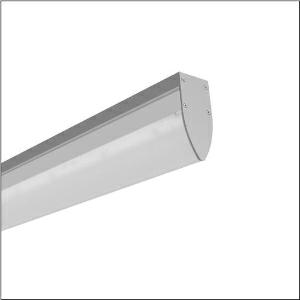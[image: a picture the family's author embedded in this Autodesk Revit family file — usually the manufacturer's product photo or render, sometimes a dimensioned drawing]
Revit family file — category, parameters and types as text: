
# Revit family: mira_r__21_td_51fr527g454a_bdf0
name_source: partatom
category: Lighting Fixtures
units: mm (PartAtom-declared; Revit-internal decimal feet)

## family parameters
Cut with Voids When Loaded = No
Host = Face
Light Source = No
Part Type = Normal
Room Calculation Point = No
Round Connector Dimension = Use Diameter
Shared = No

## types (1)
- Mira® 21 TD (1 x LED, 5500 lm, 39 W, 4000K)
    Apparent Load = 39 VA
    CIE Flux Codes = 40 68 87 81 100
    Color Rendering = 80
    Color Temperature = 4000K
    Default Elevation = 1800 mm
    Description = Mira® 21 TD, clean room luminaire, primary light control with reflector, primary optical cover: cover, of PMMA, frosted, light emission: direct distribution, primary light characteristic: symmetric, installation type: surface-mounted, LED, rated luminous flux: 5.500lm, luminous efficacy: 141lm/W, light colour: 840, colour temperature: 4000K, control gear: ECG, with terminal, 3-pole, max. 2.5mm², mains connection: 230V, AC, 50/60Hz, rated input power: 39W, luminaire housing, of sheet steel, coated, pure white (RAL 9010), length: 900mm, width: 55mm, height: 120mm, protection rating (complete): IP43, insulation class (complete): insulation class I (protective earthing), certification: CE, UKCA, permissible operating ambient temperature: -5..+40°C, standard: EN 50419, packaging unit: 1 piece
    Height = 0 mm  [stored 0 ft]
    Lamp = 1 x LED
    Lamp Light Flux = 5500 lm
    Lamp Power = 39 W
    Lamp count = 1
    Length = 900 mm
    Luminous efficacy = 141 lm/W
    Manufacturer = Siteco
    ModVariant = No
    Model = 51FR527G454A
    Mounting Place = Ceiling
    Mounting Type = Recessed
    Number of Poles = 1
    OnlyDefault = Yes
    Power Factor = 1
    Product Name = Mira® 21 TD
    Product group = clean room luminaire
    ProductGroupID = 402
    Protection Class = Protection class I
    Protection Degree = IP 43
    RLX_Detail_Level = 1
    RLX_Emergency_Light_Flux = 0 lm
    RLX_Emergency_Type = 0
    RLX_Emergency_Type_DB = No
    RlxData = <blob elided: 25101 chars, md5=ae8ec554>
    Socket = socket
    Standby Power = 0 W
    System Light Flux = 5500 lm
    System Power = 39 W
    Type Comments = Product without accessories
    Type Image = l_1007115.jpg
    URL = http://relux.com
    VarID = ---
    Voltage = 0 V
    Weight = 0.00 kg
    Width = 55 mm

note: [stored X ft] marks values corroborated as IEEE doubles in the binary element streams (Revit-internal decimal feet)

## geometry (parser evidence)
native form markers: Blend x4, Sweep x11
no freeform markers — native parametric forms only
